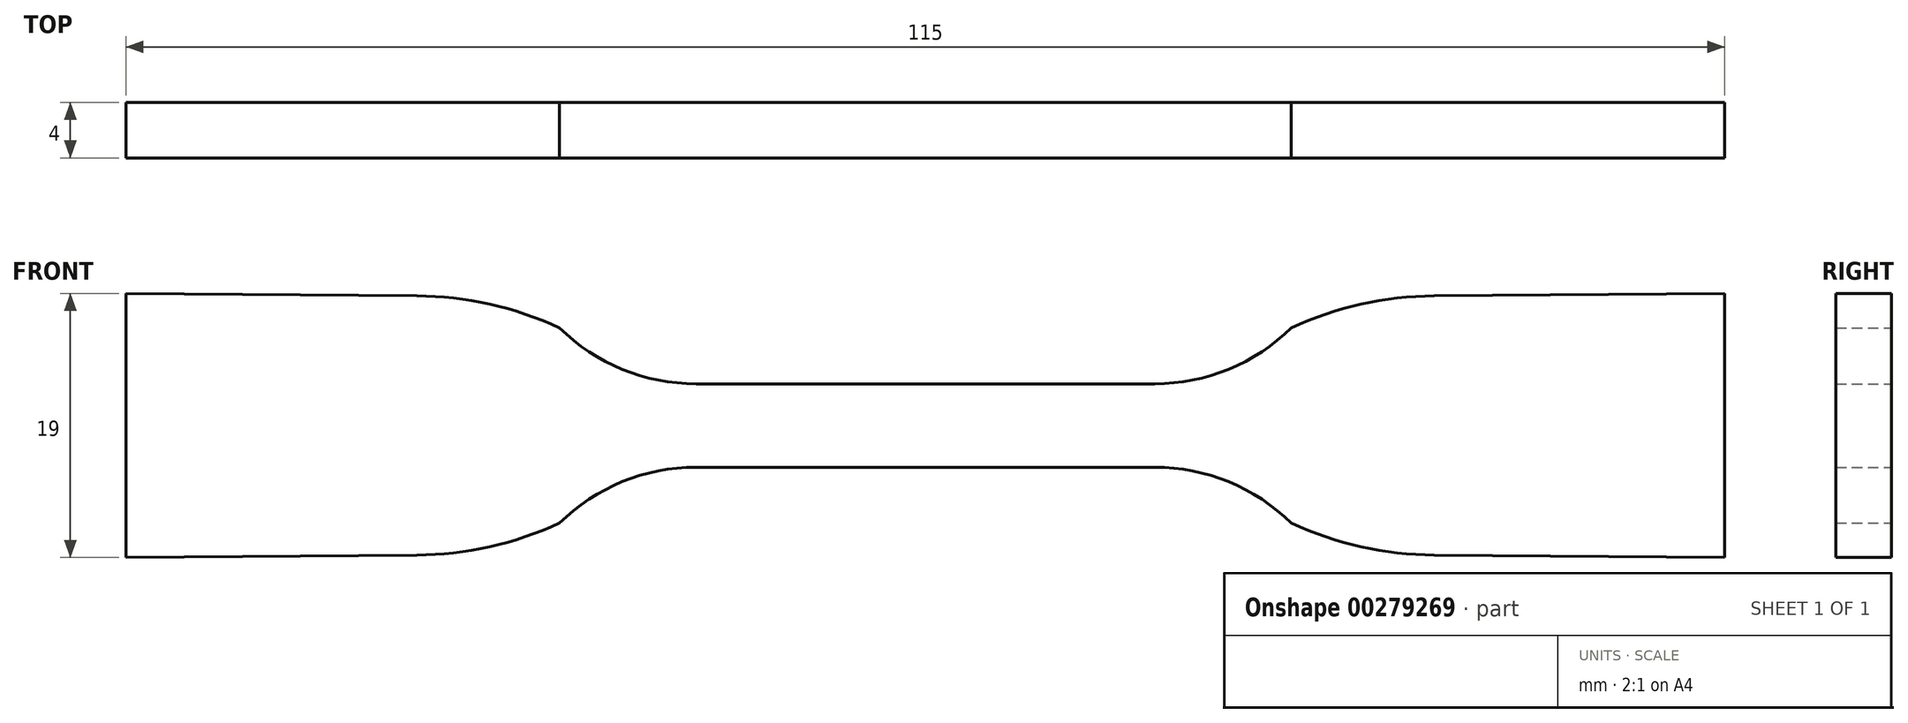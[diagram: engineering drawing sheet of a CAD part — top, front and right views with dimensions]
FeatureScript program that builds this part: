
annotation { "Feature Type Name" : "Feature", "Feature Type Description" : "" }
export const myFeature = defineFeature(function(context is Context, id is Id, definition is map)
    precondition{}
    {
        {
            var Q0;
            Q0=qCreatedBy(makeId("Front.planeOp"),FACE);
            var sketch = newSketch(context, id + "F0", { "sketchPlane" : qUnion([Q0])});
            skLineSegment(sketch, "E0", {"start": v(0, 3) * mm, "end": v(16.5, 3) * mm});
            skArc(sketch, "E1", {"start": v(16.5, 3) * mm, "mid": v(21.81, 4.05) * mm, "end": v(26.33, 7.03) * mm});
            skArc(sketch, "E2", {"start": v(36.59, 9.33) * mm, "mid": v(31.34, 8.72) * mm, "end": v(26.33, 7.03) * mm});
            skLineSegment(sketch, "E3", {"start": v(36.59, 9.33) * mm, "end": v(57.5, 9.5) * mm});
            skArc(sketch, "E4.MirrorCS", {"start": v(16.5, -3) * mm, "mid": v(21.81, -4.05) * mm, "end": v(26.33, -7.03) * mm});
            skLineSegment(sketch, "E5.MirrorCS", {"start": v(36.59, -9.33) * mm, "end": v(57.5, -9.5) * mm});
            skArc(sketch, "E6.MirrorCS", {"start": v(36.59, -9.33) * mm, "mid": v(31.34, -8.72) * mm, "end": v(26.33, -7.03) * mm});
            skLineSegment(sketch, "E7.MirrorCS", {"start": v(0, -3) * mm, "end": v(16.5, -3) * mm});
            skLineSegment(sketch, "E8.MirrorCS", {"start": v(-36.59, 9.33) * mm, "end": v(-57.5, 9.5) * mm});
            skArc(sketch, "E9.MirrorCS", {"start": v(-16.5, 3) * mm, "mid": v(-21.81, 4.05) * mm, "end": v(-26.33, 7.03) * mm});
            skArc(sketch, "E10.MirrorCS", {"start": v(-16.5, -3) * mm, "mid": v(-21.81, -4.05) * mm, "end": v(-26.33, -7.03) * mm});
            skLineSegment(sketch, "E11.MirrorCS", {"start": v(0, 3) * mm, "end": v(-16.5, 3) * mm});
            skArc(sketch, "E12.MirrorCS", {"start": v(-36.59, 9.33) * mm, "mid": v(-31.34, 8.72) * mm, "end": v(-26.33, 7.03) * mm});
            skLineSegment(sketch, "E13.MirrorCS", {"start": v(0, -3) * mm, "end": v(-16.5, -3) * mm});
            skArc(sketch, "E14.MirrorCS", {"start": v(-36.59, -9.33) * mm, "mid": v(-31.34, -8.72) * mm, "end": v(-26.33, -7.03) * mm});
            skLineSegment(sketch, "E15.MirrorCS", {"start": v(-36.59, -9.33) * mm, "end": v(-57.5, -9.5) * mm});
            skLineSegment(sketch, "E16", {"start": v(57.5, 9.5) * mm, "end": v(57.5, -9.5) * mm});
            skLineSegment(sketch, "E17", {"start": v(-57.5, -9.5) * mm, "end": v(-57.5, 9.5) * mm});
            skSolve(sketch);
        }
        {
            var Q0;
            Q0 = qSketchRegion(id + "F0", true);
            extrude(context, id + "F1", {"entities" : qUnion([Q0]), "endBound" : BoundingType.SYMMETRIC, "depth" : 4 * mm});
        }
    });
